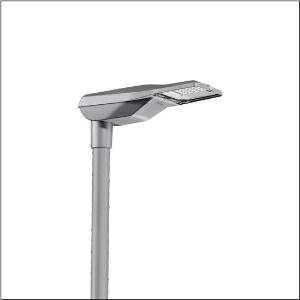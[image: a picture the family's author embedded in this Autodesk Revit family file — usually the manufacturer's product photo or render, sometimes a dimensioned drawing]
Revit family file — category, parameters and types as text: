
# Revit family: streetlight_sl_21_iq_micro___p0_5a_5xe1v31g08db_d973
name_source: partatom
category: Lighting Fixtures
units: mm (PartAtom-declared; Revit-internal decimal feet)

## family parameters
Cut with Voids When Loaded = No
Host = Face
Light Source = No
Part Type = Normal
Room Calculation Point = No
Round Connector Dimension = Use Diameter
Shared = No

## types (1)
- --- (1 x LED, 4660 lm, 36.4 W, 3000K)
    Apparent Load = 36 VA
    CIE Flux Codes = 37 73 96 100 100
    Color Rendering = 70
    Color Temperature = 3000K
    Default Elevation = 1800 mm
    Description = Streetlight SL 21 iQ micro, mast luminaire, primary light control with lens, of PMMA, primary optical cover: cover, of toughened safety glass, transparent, light distribution: P0.5a, light emission: direct distribution, primary light characteristic: asymmetric, installation type: post-top, side-entry, LED, High Power LED, rated luminous flux: 4.660lm, luminous efficacy: 128lm/W, light colour: 730, colour temperature: 3000K, control gear: iQ Street-Remote, control: pre-setting: linear dimming characteristic, Street-Remote, Auto-Match, Temp-Guard, Lumen-Switch, Night-Set, Smart-Wire, Light-Fading, Desk-Remote (wireless, voltage-free reading and setting of iQ features in the workshop via application-optimized NFC function/RFID function), optimised constant luminous flux control (CLO 2.0), mains connection: 220..240V, AC, 50/60Hz, start of lifetime: 36W, end of service life: 38W, reduction: 16W, luminaire housing, of diecast aluminium, powder-coated, SITECO metallic grey (DB 702S), corrosivity category C5 high according to DIN EN ISO 12944, please order mast flange separately, inclination adjustable: 0°, 5°, 10°, 15°, sealing non-destructively replaceable, multi-level sealing system, length: 528mm, width: 235mm, height: 110mm, mast flange for spigot size: 42mm (side-entry): 5XC10008XM4, 60/48mm (side-entry/post-top): 5XC10108XM2, 76/60mm (side-entry/post-top): 5XC10108XM1, protection rating (complete): IP66, insulation class (complete): insulation class II (safety insulation), certification: CE, ENEC, ENEC+, VDE, impact resistance: IK10, permissible operating ambient temperature for outdoor applications: -40..+50°C, standard-compliant lighting for roads and squares, packaging unit: 1 piece

Light Distribution: P0.5a
    Height = 110 mm
    Lamp = 1 x LED
    Lamp Light Flux = 4660 lm
    Lamp Power = 36.4 W
    Lamp count = 1
    Length = 528 mm
    Luminous efficacy = 128 lm/W
    Manufacturer = Siteco
    ModVariant = No
    Model = 5XE1V31G08DB
    Mounting Place = Pole
    Mounting Type = Pole top
    Number of Poles = 1
    OnlyDefault = Yes
    Power Factor = 1
    Product Name = Streetlight SL 21 iQ micro | P0.5a
    Product group = mast luminaire | pylon top
    ProductGroupID = 6100
    Protection Class = Protection class II
    Protection Degree = IP 66
    RLX_Detail_Level = 1
    RLX_Emergency_Light_Flux = 0 lm
    RLX_Emergency_Type = 0
    RLX_Emergency_Type_DB = No
    RlxData = <blob elided: 98445 chars, md5=ef7ac5df>
    Socket = socket
    Standby Power = 0 W
    System Light Flux = 4660 lm
    System Power = 36 W
    Type Comments = factory setting: luminous flux: 100 % | dim-lin: 254 | 715 mA
    Type Image = l_1006881.jpg
    URL = http://relux.com
    VarID = @adj_079669
    Voltage = 0 V
    Weight = 0.00 kg
    Width = 235 mm

## geometry (parser evidence)
native form markers: Blend x4, Sweep x11
no freeform markers — native parametric forms only
